# Revit family: Rohrschelle Maxima PSM, M16, Ø250-255, Gummi
name_source: partatom
category: HLS-Bauteile
revit_build: Autodesk Revit 2018 (Build: 20190510_1515(x64)
units: mm (PartAtom-declared; Revit-internal decimal feet)

## family parameters
Arbeitsebenenbasiert = Ja
Beim Laden mit Abzugskörper schneiden = Nein
Bemaßung runder Anschluss = Durchmesser verwenden
Gemeinsam genutzt = Ja
Immer vertikal = Nein
Raumberechnungspunkt = Nein
Teiletyp = Normal

## types (1)
- Maxima PSM, M16, Ø250-255, Gummi
    A = 30 mm  [stored 0.0984252 ft]
    AB = 5 mm  [stored 0.0164042 ft]
    Achsabstand = 310 mm
    Anschluss = M16
    Anschlußhöhe = 30 mm
    Artikelnummer = 0081833
    B = 339 mm  [stored 1.1122 ft]
    Bauart = zweiteilig
    Baustoffklasse = B2
    Brandschutz = RAL-GZ 656
    Breite = 331 mm  [stored 1.08596 ft]
    Breite Material = 35 mm
    D = 255 mm  [stored 0.836614 ft]
    D0 = 267 mm  [stored 0.875984 ft]
    DF1 = 30 mm  [stored 0.0984252 ft]
    DF2 = 34 mm
    DS = 6 mm  [stored 0.019685 ft]
    DVS = 18 mm  [stored 0.0590551 ft]
    Dmax = 255 mm  [stored 0.836614 ft]
    Dmin = 250 mm  [stored 0.82021 ft]
    Dämmstärke = 6 mm  [stored 0.019685 ft]
    EAN = 4250928455826
    Fabrikat = MEFA
    Farbe Schalldämmeinlage = Schwarz
    Firma = MEFA Befestigungs- und Montagesysteme GmbH
    Gewicht = 1.40 kg
    Gewicht pro Bauteil = 1.40 kg
    H = 295 mm  [stored 0.967848 ft]
    HGA = 20 mm  [stored 0.0656168 ft]
    Kurztext1 = Rohrschelle Maxima PSM 35x4
    Kurztext2 = 250 - 255 mm M16 TPE
    MB = 35 mm  [stored 0.114829 ft]
    MD = 4 mm  [stored 0.0131234 ft]
    Material = Stahl
    Material Schalldämmeinlage = TPE
    Materialmaße = 35x4,0 mm
    Materialname = S235
    Mengeneinheit = St
    Nennweite DN Rohr = 0 mm  [stored 0 ft]
    Oberflaeche = galvanisch verzinkt
    R = 134 mm
    RM = 138 mm
    Rohraußendurchmesser = 0 mm  [stored 0 ft]
    Rohraußendurchmesser Zoll = Zoll
    S = 309 mm  [stored 1.01378 ft]
    Schalldämmeinlage = Gummi TPE
    Stärke Material = 4 mm  [stored 0.0131234 ft]
    Verschluss = Pendelsteckmuttern
    Verschluss-Schraube = M10
    Vorgabe-Ansicht = 1219 mm
    max. Höhe = 286 mm
    max. Rohraußendurchmesser = 255 mm  [stored 0.836614 ft]
    max. Temperaturbeständigkeit = 100 °C
    max. zul. Last = 5.00 kN
    max. zul. Last horizontal = 0.00 kN
    max. zul. Last vertikal = 0.00 kN
    min. Rohraußendurchmesser = 250 mm  [stored 0.82021 ft]
    vpe = 1

note: [stored X ft] marks values corroborated as IEEE doubles in the binary element streams (Revit-internal decimal feet)

## geometry (parser evidence)
native form markers: Sweep x3
no freeform markers — native parametric forms only
